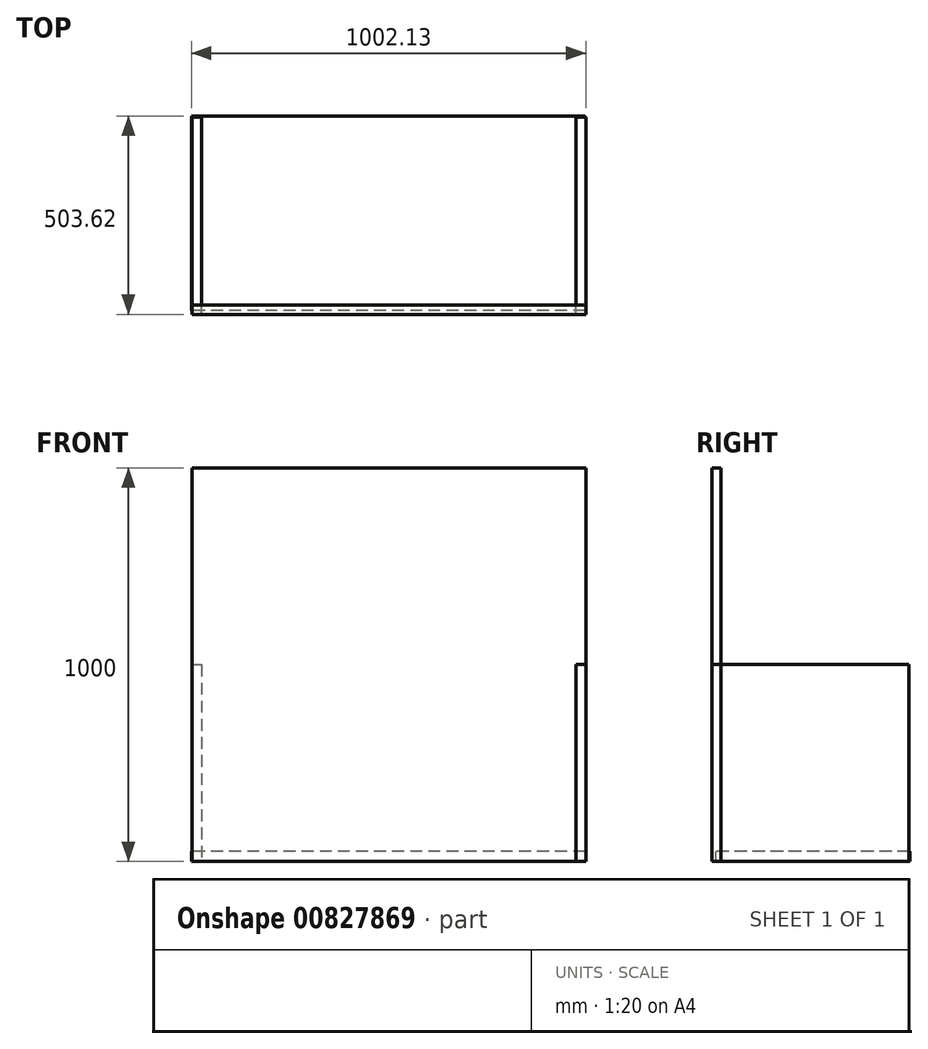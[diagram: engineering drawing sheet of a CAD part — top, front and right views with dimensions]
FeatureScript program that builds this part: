
annotation { "Feature Type Name" : "Feature", "Feature Type Description" : "" }
export const myFeature = defineFeature(function(context is Context, id is Id, definition is map)
    precondition{}
    {
        {
            var Q0;
            Q0=qCreatedBy(makeId("Top.planeOp"),FACE);
            var sketch = newSketch(context, id + "F0", { "sketchPlane" : qUnion([Q0])});
            skLineSegment(sketch, "E0.bottom", {"start": v(-1410.16, 946.43) * mm, "end": v(1129.84, 946.43) * mm});
            skLineSegment(sketch, "E0.top", {"start": v(-1410.16, -922.62) * mm, "end": v(1129.84, -922.62) * mm});
            skLineSegment(sketch, "E0.left", {"start": v(-1410.16, 946.43) * mm, "end": v(-1410.16, -922.62) * mm});
            skLineSegment(sketch, "E0.right", {"start": v(1129.84, 946.43) * mm, "end": v(1129.84, -922.62) * mm});
            skSolve(sketch);
        }
        {
            var Q0;
            Q0=qCreatedBy(makeId("Top.planeOp"),FACE);
            var sketch = newSketch(context, id + "F1", { "sketchPlane" : qUnion([Q0])});
            skLineSegment(sketch, "E1.bottom", {"start": v(-308.9, 303.6) * mm, "end": v(691.1, 303.6) * mm});
            skLineSegment(sketch, "E1.top", {"start": v(-308.9, -196.4) * mm, "end": v(691.1, -196.4) * mm});
            skLineSegment(sketch, "E1.left", {"start": v(-308.9, 303.6) * mm, "end": v(-308.9, -196.4) * mm});
            skLineSegment(sketch, "E1.right", {"start": v(691.1, 303.6) * mm, "end": v(691.1, -196.4) * mm});
            skSolve(sketch);
        }
        {
            var Q0;
            Q0=makeQuery(id+"F1.imprint","IMPRINT",FACE,{"disambiguationData":[TD([[makeQuery(id+"F1.imprint","IMPRINT",EDGE,{"derivedFrom":sQuery(id+"F1.wireOp",EDGE,"E1.bottom")}),-1.0]])]});
            var sketch = newSketch(context, id + "F2", { "sketchPlane" : qUnion([Q0])});
            skLineSegment(sketch, "E2.bottom", {"start": v(-308.95, -196.5) * mm, "end": v(-285.17, -196.5) * mm});
            skLineSegment(sketch, "E2.top", {"start": v(-308.95, 303.84) * mm, "end": v(-285.17, 303.84) * mm});
            skLineSegment(sketch, "E2.left", {"start": v(-308.95, -196.5) * mm, "end": v(-308.95, 303.84) * mm});
            skLineSegment(sketch, "E2.right", {"start": v(-285.17, -196.5) * mm, "end": v(-285.17, 303.84) * mm});
            skSolve(sketch);
        }
        {
            var Q0;
            Q0 = qSketchRegion(id + "F2", true);
            extrude(context, id + "F3", {"entities" : qUnion([Q0]), "depth" : 500 * mm, "offsetDistance" : 25 * mm});
        }
        {
            var Q0;
            Q0=makeQuery(id+"F0.imprint","IMPRINT",FACE,{"disambiguationData":[TD([[makeQuery(id+"F0.imprint","IMPRINT",EDGE,{"derivedFrom":sQuery(id+"F0.wireOp",EDGE,"E0.bottom")}),-1.0]])]});
            var sketch = newSketch(context, id + "F4", { "sketchPlane" : qUnion([Q0])});
            skLineSegment(sketch, "E3.bottom", {"start": v(691.16, -196.74) * mm, "end": v(666.58, -196.74) * mm});
            skLineSegment(sketch, "E3.top", {"start": v(691.16, 304.48) * mm, "end": v(666.58, 304.48) * mm});
            skLineSegment(sketch, "E3.left", {"start": v(691.16, -196.74) * mm, "end": v(691.16, 304.48) * mm});
            skLineSegment(sketch, "E3.right", {"start": v(666.58, -196.74) * mm, "end": v(666.58, 304.48) * mm});
            skSolve(sketch);
        }
        {
            var Q0;
            Q0 = qSketchRegion(id + "F4", true);
            extrude(context, id + "F5", {"entities" : qUnion([Q0]), "depth" : 500 * mm, "offsetDistance" : 25 * mm});
        }
        {
            var Q0;
            Q0=makeQuery(id+"F1.imprint","IMPRINT",FACE,{"disambiguationData":[TD([[makeQuery(id+"F1.imprint","IMPRINT",EDGE,{"derivedFrom":sQuery(id+"F1.wireOp",EDGE,"E1.bottom")}),-1.0]])]});
            var sketch = newSketch(context, id + "F6", { "sketchPlane" : qUnion([Q0])});
            skLineSegment(sketch, "E4.bottom", {"start": v(-309.14, -196.74) * mm, "end": v(691.16, -196.74) * mm});
            skLineSegment(sketch, "E4.top", {"start": v(-309.14, -173.23) * mm, "end": v(691.16, -173.23) * mm});
            skLineSegment(sketch, "E4.left", {"start": v(-309.14, -196.74) * mm, "end": v(-309.14, -173.23) * mm});
            skLineSegment(sketch, "E4.right", {"start": v(691.16, -196.74) * mm, "end": v(691.16, -173.23) * mm});
            skSolve(sketch);
        }
        {
            var Q0;
            Q0 = qSketchRegion(id + "F6", true);
            extrude(context, id + "F7", {"entities" : qUnion([Q0]), "depth" : 1000 * mm, "offsetDistance" : 25 * mm});
        }
        {
            var Q0;
            Q0=makeQuery(id+"F1.imprint","IMPRINT",FACE,{"disambiguationData":[TD([[makeQuery(id+"F1.imprint","IMPRINT",EDGE,{"derivedFrom":sQuery(id+"F1.wireOp",EDGE,"E1.bottom")}),-1.0]])]});
            var sketch = newSketch(context, id + "F8", { "sketchPlane" : qUnion([Q0])});
            skLineSegment(sketch, "E5.bottom", {"start": v(689.24, 306.88) * mm, "end": v(-310.97, 306.88) * mm});
            skLineSegment(sketch, "E5.top", {"start": v(689.24, -187.21) * mm, "end": v(-310.97, -187.21) * mm});
            skLineSegment(sketch, "E5.left", {"start": v(689.24, 306.88) * mm, "end": v(689.24, -187.21) * mm});
            skLineSegment(sketch, "E5.right", {"start": v(-310.97, 306.88) * mm, "end": v(-310.97, -187.21) * mm});
            skSolve(sketch);
        }
        {
            var Q0;
            Q0 = qSketchRegion(id + "F8", true);
            extrude(context, id + "F9", {"entities" : qUnion([Q0]), "depth" : 25 * mm, "offsetDistance" : 25 * mm});
        }
    });
